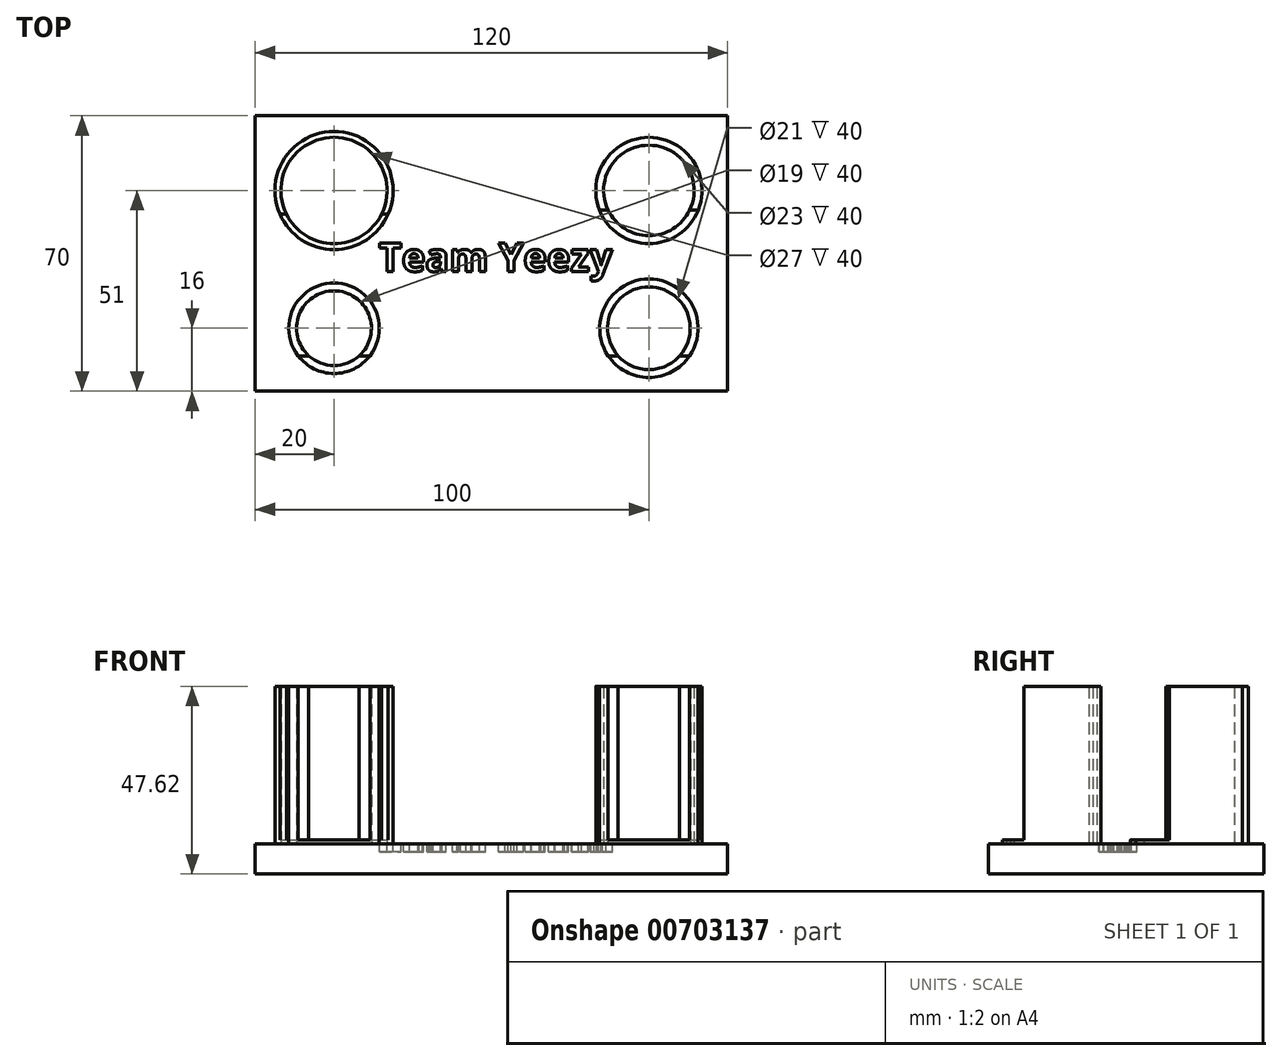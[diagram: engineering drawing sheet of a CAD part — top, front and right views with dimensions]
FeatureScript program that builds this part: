
annotation { "Feature Type Name" : "Feature", "Feature Type Description" : "" }
export const myFeature = defineFeature(function(context is Context, id is Id, definition is map)
    precondition{}
    {
        {
            var Q0;
            Q0=qCreatedBy(makeId("Top.planeOp"),FACE);
            var sketch = newSketch(context, id + "F0", { "sketchPlane" : qUnion([Q0])});
            skLineSegment(sketch, "E0", {"start": v(-60, 35) * mm, "end": v(-60, -35) * mm});
            skLineSegment(sketch, "E1", {"start": v(-60, -35) * mm, "end": v(60, -35) * mm});
            skLineSegment(sketch, "E2", {"start": v(60, -35) * mm, "end": v(60, 35) * mm});
            skLineSegment(sketch, "E3", {"start": v(60, 35) * mm, "end": v(-60, 35) * mm});
            skSolve(sketch);
        }
        {
            var Q0;
            Q0 = qSketchRegion(id + "F0", true);
            extrude(context, id + "F1", {"entities" : qUnion([Q0]), "depth" : 7.62 * mm, "offsetDistance" : 25.4 * mm});
        }
        {
            var Q0;
            Q0=makeQuery(id+"F1.opExtrude","CAP_FACE",FACE,{"disambiguationData":[OSD([sQuery(id+"F0.wireOp",EDGE,"E0"),sQuery(id+"F0.wireOp",EDGE,"E1"),sQuery(id+"F0.wireOp",EDGE,"E2"),sQuery(id+"F0.wireOp",EDGE,"E3")])],"isStart":false});
            var sketch = newSketch(context, id + "F2", { "sketchPlane" : qUnion([Q0])});
            skCircle(sketch, "E4", {"center": v(-40, 16) * mm, "radius": 13.5 * mm});
            skCircle(sketch, "E5", {"center": v(-40, 16) * mm, "radius": 15 * mm});
            skCircle(sketch, "E6", {"center": v(40, 16) * mm, "radius": 11.5 * mm});
            skCircle(sketch, "E7", {"center": v(40, 16) * mm, "radius": 13.5 * mm});
            skCircle(sketch, "E8", {"center": v(-40, -19) * mm, "radius": 9.5 * mm});
            skCircle(sketch, "E9", {"center": v(-40, -19) * mm, "radius": 11.5 * mm});
            skCircle(sketch, "E10", {"center": v(40, -19) * mm, "radius": 10.5 * mm});
            skCircle(sketch, "E11", {"center": v(40, -19) * mm, "radius": 12.5 * mm});
            skSolve(sketch);
        }
        {
            var Q0;
            Q0=makeQuery(id+"F2.imprint","IMPRINT",FACE,{"disambiguationData":[TD([[makeQuery(id+"F2.imprint","IMPRINT",EDGE,{"derivedFrom":sQuery(id+"F2.wireOp",EDGE,"E4")}),-1.0]])]});
            extrude(context, id + "F3", {"entities" : qUnion([Q0]), "operationType" : NewBodyOperationType.ADD, "depth" : 40 * mm, "offsetDistance" : 25 * mm});
        }
        {
            var Q0;
            Q0=makeQuery(id+"F2.imprint","IMPRINT",FACE,{"disambiguationData":[TD([[makeQuery(id+"F2.imprint","IMPRINT",EDGE,{"derivedFrom":sQuery(id+"F2.wireOp",EDGE,"E6")}),-1.0]])]});
            extrude(context, id + "F4", {"entities" : qUnion([Q0]), "operationType" : NewBodyOperationType.ADD, "depth" : 40 * mm, "offsetDistance" : 25 * mm});
        }
        {
            var Q0;
            Q0=makeQuery(id+"F2.imprint","IMPRINT",FACE,{"disambiguationData":[TD([[makeQuery(id+"F2.imprint","IMPRINT",EDGE,{"derivedFrom":sQuery(id+"F2.wireOp",EDGE,"E10")}),-1.0]])]});
            extrude(context, id + "F5", {"entities" : qUnion([Q0]), "operationType" : NewBodyOperationType.ADD, "depth" : 40 * mm, "offsetDistance" : 25 * mm});
        }
        {
            var Q0;
            Q0=makeQuery(id+"F2.imprint","IMPRINT",FACE,{"disambiguationData":[TD([[makeQuery(id+"F2.imprint","IMPRINT",EDGE,{"derivedFrom":sQuery(id+"F2.wireOp",EDGE,"E8")}),-1.0]])]});
            extrude(context, id + "F6", {"entities" : qUnion([Q0]), "operationType" : NewBodyOperationType.ADD, "depth" : 40 * mm, "offsetDistance" : 25 * mm});
        }
        {
            var Q0;
            Q0=makeQuery(id+"F3.opExtrude","CAP_FACE",FACE,{"disambiguationData":[OSD([sQuery(id+"F2.wireOp",EDGE,"E4"),sQuery(id+"F2.wireOp",EDGE,"E5")])],"isStart":false});
            var sketch = newSketch(context, id + "F7", { "sketchPlane" : qUnion([Q0])});
            skLineSegment(sketch, "E12.bottom", {"start": v(-55.9, 10) * mm, "end": v(-24.1, 10) * mm});
            skLineSegment(sketch, "E12.top", {"start": v(-55.9, 0.3) * mm, "end": v(-24.1, 0.3) * mm});
            skLineSegment(sketch, "E12.left", {"start": v(-55.9, 10) * mm, "end": v(-55.9, 0.3) * mm});
            skLineSegment(sketch, "E12.right", {"start": v(-24.1, 10) * mm, "end": v(-24.1, 0.3) * mm});
            skSolve(sketch);
        }
        {
            var Q0;
            {var subQ0=sQuery(id+"F7.wireOp",EDGE,"E12.bottom");var subQ1=makeQuery(id+"F3.opExtrude","CAP_EDGE",EDGE,{"disambiguationData":[OSD([sQuery(id+"F2.wireOp",EDGE,"E5")])],"isStart":false});var subQ2=makeQuery(id+"F7.imprint","INTERSECT",VERTEX,{"disambiguationData":[OD(0.0)],"derivedFrom":[subQ1,subQ0]});Q0=makeQuery(id+"F7.imprint","IMPRINT",FACE,{"disambiguationData":[TD([[makeQuery(id+"F7.imprint","IMPRINT",EDGE,{"disambiguationData":[TD([[subQ2,-1.0]])],"derivedFrom":subQ0}),-1.0]])]});}
            extrude(context, id + "F8", {"entities" : qUnion([Q0]), "operationType" : NewBodyOperationType.REMOVE, "oppositeDirection" : true, "depth" : 39 * mm, "offsetDistance" : 25 * mm});
        }
        {
            var Q0;
            Q0=makeQuery(id+"F4.opExtrude","CAP_FACE",FACE,{"disambiguationData":[OSD([sQuery(id+"F2.wireOp",EDGE,"E6"),sQuery(id+"F2.wireOp",EDGE,"E7")])],"isStart":false});
            var sketch = newSketch(context, id + "F9", { "sketchPlane" : qUnion([Q0])});
            skLineSegment(sketch, "E13.bottom", {"start": v(27, 11) * mm, "end": v(53, 11) * mm});
            skLineSegment(sketch, "E13.top", {"start": v(27, 4) * mm, "end": v(53, 4) * mm});
            skLineSegment(sketch, "E13.left", {"start": v(27, 11) * mm, "end": v(27, 4) * mm});
            skLineSegment(sketch, "E13.right", {"start": v(53, 11) * mm, "end": v(53, 4) * mm});
            skSolve(sketch);
        }
        {
            var Q0;
            {var subQ0=sQuery(id+"F9.wireOp",EDGE,"E13.bottom");var subQ1=makeQuery(id+"F4.opExtrude","CAP_EDGE",EDGE,{"disambiguationData":[OSD([sQuery(id+"F2.wireOp",EDGE,"E7")])],"isStart":false});var subQ2=makeQuery(id+"F9.imprint","INTERSECT",VERTEX,{"disambiguationData":[OD(0.0)],"derivedFrom":[subQ1,subQ0]});Q0=makeQuery(id+"F9.imprint","IMPRINT",FACE,{"disambiguationData":[TD([[makeQuery(id+"F9.imprint","IMPRINT",EDGE,{"disambiguationData":[TD([[subQ2,-1.0]])],"derivedFrom":subQ0}),-1.0]])]});}
            extrude(context, id + "F10", {"entities" : qUnion([Q0]), "operationType" : NewBodyOperationType.REMOVE, "oppositeDirection" : true, "depth" : 39 * mm, "offsetDistance" : 25 * mm});
        }
        {
            var Q0;
            Q0=makeQuery(id+"F6.opExtrude","CAP_FACE",FACE,{"disambiguationData":[OSD([sQuery(id+"F2.wireOp",EDGE,"E8"),sQuery(id+"F2.wireOp",EDGE,"E9")])],"isStart":false});
            var sketch = newSketch(context, id + "F11", { "sketchPlane" : qUnion([Q0])});
            skLineSegment(sketch, "E14.bottom", {"start": v(-53, -26) * mm, "end": v(-29.05, -26) * mm});
            skLineSegment(sketch, "E14.top", {"start": v(-53, -30) * mm, "end": v(-29.05, -30) * mm});
            skLineSegment(sketch, "E14.left", {"start": v(-53, -26) * mm, "end": v(-53, -30) * mm});
            skLineSegment(sketch, "E14.right", {"start": v(-29.05, -26) * mm, "end": v(-29.05, -30) * mm});
            skSolve(sketch);
        }
        {
            var Q0;
            {var subQ0=sQuery(id+"F11.wireOp",EDGE,"E14.bottom");var subQ1=makeQuery(id+"F6.opExtrude","CAP_EDGE",EDGE,{"disambiguationData":[OSD([sQuery(id+"F2.wireOp",EDGE,"E9")])],"isStart":false});var subQ2=makeQuery(id+"F11.imprint","INTERSECT",VERTEX,{"disambiguationData":[OD(0.0)],"derivedFrom":[subQ1,subQ0]});Q0=makeQuery(id+"F11.imprint","IMPRINT",FACE,{"disambiguationData":[TD([[makeQuery(id+"F11.imprint","IMPRINT",EDGE,{"disambiguationData":[TD([[subQ2,-1.0]])],"derivedFrom":subQ0}),-1.0]])]});}
            extrude(context, id + "F12", {"entities" : qUnion([Q0]), "operationType" : NewBodyOperationType.REMOVE, "oppositeDirection" : true, "depth" : 39 * mm, "offsetDistance" : 25 * mm});
        }
        {
            var Q0;
            Q0=makeQuery(id+"F5.opExtrude","CAP_FACE",FACE,{"disambiguationData":[OSD([sQuery(id+"F2.wireOp",EDGE,"E10"),sQuery(id+"F2.wireOp",EDGE,"E11")])],"isStart":false});
            var sketch = newSketch(context, id + "F13", { "sketchPlane" : qUnion([Q0])});
            skLineSegment(sketch, "E15.bottom", {"start": v(28, -26) * mm, "end": v(52, -26) * mm});
            skLineSegment(sketch, "E15.top", {"start": v(28, -32) * mm, "end": v(52, -32) * mm});
            skLineSegment(sketch, "E15.left", {"start": v(28, -26) * mm, "end": v(28, -32) * mm});
            skLineSegment(sketch, "E15.right", {"start": v(52, -26) * mm, "end": v(52, -32) * mm});
            skSolve(sketch);
        }
        {
            var Q0;
            {var subQ0=sQuery(id+"F13.wireOp",EDGE,"E15.bottom");var subQ1=makeQuery(id+"F5.opExtrude","CAP_EDGE",EDGE,{"disambiguationData":[OSD([sQuery(id+"F2.wireOp",EDGE,"E11")])],"isStart":false});var subQ2=makeQuery(id+"F13.imprint","INTERSECT",VERTEX,{"disambiguationData":[OD(0.0)],"derivedFrom":[subQ1,subQ0]});Q0=makeQuery(id+"F13.imprint","IMPRINT",FACE,{"disambiguationData":[TD([[makeQuery(id+"F13.imprint","IMPRINT",EDGE,{"disambiguationData":[TD([[subQ2,-1.0]])],"derivedFrom":subQ0}),-1.0]])]});}
            extrude(context, id + "F14", {"entities" : qUnion([Q0]), "operationType" : NewBodyOperationType.REMOVE, "oppositeDirection" : true, "depth" : 39 * mm, "offsetDistance" : 25 * mm});
        }
        {
            var Q0;
            Q0=makeQuery(id+"F2.imprint","IMPRINT",FACE,{"disambiguationData":[TD([[makeQuery(id+"F2.imprint","IMPRINT",EDGE,{"derivedFrom":sQuery(id+"F2.wireOp",EDGE,"E5")}),-1.0]])]});
            var sketch = newSketch(context, id + "F15", { "sketchPlane" : qUnion([Q0])});
            skText(sketch, "E16", { "text": "Team Yeezy", "fontName": "OpenSans-Bold.ttf"});
            const initialGuessF15  = {"E16": [-0.02863, -0.00458, 1, 0, 0.00727]};
            skSetInitialGuess(sketch, initialGuessF15);
            skSolve(sketch);
        }
        {
            var Q0;
            Q0 = qSketchRegion(id + "F15", true);
            extrude(context, id + "F16", {"entities" : qUnion([Q0]), "operationType" : NewBodyOperationType.REMOVE, "oppositeDirection" : true, "depth" : 2 * mm, "offsetDistance" : 25 * mm});
        }
        {
            var Q0;
            {var subQ0=sQuery(id+"F2.wireOp",EDGE,"E7");Q0=makeQuery(id+"F10.boolean.opBoolean","SPLIT",FACE,{"disambiguationData":[TD([makeQuery(id+"F10.opExtrude","SWEPT_FACE",FACE,{"disambiguationData":[OSD([sQuery(id+"F9.wireOp",EDGE,"E13.top")])]})])],"derivedFrom":makeQuery(id+"F4.opExtrude","CAP_FACE",FACE,{"disambiguationData":[OSD([sQuery(id+"F2.wireOp",EDGE,"E6"),subQ0])],"isStart":false})});}
            extrude(context, id + "F17", {"entities" : qUnion([Q0]), "operationType" : NewBodyOperationType.ADD, "depth" : 39 * mm, "offsetDistance" : 25 * mm});
        }
        {
            var Q0;
            {var subQ0=sQuery(id+"F2.wireOp",EDGE,"E9");Q0=makeQuery(id+"F12.boolean.opBoolean","SPLIT",FACE,{"disambiguationData":[TD([makeQuery(id+"F12.opExtrude","SWEPT_FACE",FACE,{"disambiguationData":[OSD([sQuery(id+"F11.wireOp",EDGE,"E14.top")])]})])],"derivedFrom":makeQuery(id+"F6.opExtrude","CAP_FACE",FACE,{"disambiguationData":[OSD([sQuery(id+"F2.wireOp",EDGE,"E8"),subQ0])],"isStart":false})});}
            extrude(context, id + "F18", {"entities" : qUnion([Q0]), "operationType" : NewBodyOperationType.REMOVE, "oppositeDirection" : true, "depth" : 39 * mm, "offsetDistance" : 25 * mm});
        }
        {
            var Q0;
            Q0=makeQuery(id+"F17.opExtrude","CAP_FACE",FACE,{"disambiguationData":[OSD([sQuery(id+"F2.wireOp",EDGE,"E6"),sQuery(id+"F2.wireOp",EDGE,"E7")])],"isStart":false});
            extrude(context, id + "F19", {"entities" : qUnion([Q0]), "operationType" : NewBodyOperationType.REMOVE, "oppositeDirection" : true, "depth" : 39 * mm, "offsetDistance" : 25 * mm});
        }
        {
            var Q0;
            Q0=makeQuery(id+"F19.boolean.opBoolean","COPY",FACE,{"derivedFrom":makeQuery(id+"F19.opExtrude","CAP_FACE",FACE,{"disambiguationData":[OSD([sQuery(id+"F2.wireOp",EDGE,"E6"),sQuery(id+"F2.wireOp",EDGE,"E7")])],"isStart":false})});
            extrude(context, id + "F20", {"entities" : qUnion([Q0]), "operationType" : NewBodyOperationType.REMOVE, "oppositeDirection" : true, "depth" : 39 * mm, "offsetDistance" : 25 * mm});
        }
    });
